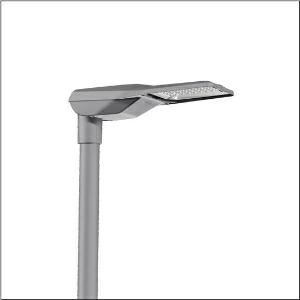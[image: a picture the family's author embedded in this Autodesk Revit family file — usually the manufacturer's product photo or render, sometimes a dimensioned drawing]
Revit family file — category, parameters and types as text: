
# Revit family: streetlight_sl_21_iq_mini___st0_5a_5xe2b31g08gb_b1a9
name_source: partatom
category: Lighting Fixtures
units: mm (PartAtom-declared; Revit-internal decimal feet)

## family parameters
Cut with Voids When Loaded = No
Host = Face
Light Source = No
Part Type = Normal
Room Calculation Point = No
Round Connector Dimension = Use Diameter
Shared = No

## types (1)
- --- (1 x LED, 5680 lm, 37.1 W, 3000K)
    Apparent Load = 37 VA
    CIE Flux Codes = 41 75 97 100 100
    Color Rendering = 70
    Color Temperature = 3000K
    Default Elevation = 1800 mm
    Description = Streetlight SL 21 iQ mini, mast luminaire, primary light control with lens, of PMMA, primary optical cover: cover, of toughened safety glass, transparent, light distribution: ST0.5a, light emission: direct distribution, primary light characteristic: asymmetric, installation type: post-top, side-entry, LED, High Power LED, rated luminous flux: 5.680lm, luminous efficacy: 153lm/W, light colour: 730, colour temperature: 3000K, control: Street-Remote, Auto-Match, Temp-Guard, Lumen-Switch, Night-Set, Smart-Wire, Light-Fading, Desk-Remote (wireless, voltage-free reading and setting of iQ features in the workshop via application-optimized NFC function/RFID function), optimised constant luminous flux control (CLO 2.0), presetting dimming linear, mains connection: 220..240V, AC, 50/60Hz, start of lifetime: 37W, end of service life: 39W, reduction: 18W, luminaire housing, of diecast aluminium, powder-coated, Siteco® metallic grey (DB 702S), corrosivity category C5 mid according to DIN EN ISO 12944, please order mast flange separately, inclination adjustable: 0°, 5°, 10°, 15°, sealing non-destructively replaceable, multi-level sealing system, length: 628mm, width: 235mm, height: 110mm, mast flange for spigot size: 42mm (side-entry): 5XC10008XM4, 60/48mm (side-entry/post-top): 5XC10108XM2, 76/60mm (side-entry/post-top): 5XC10108XM1, protection rating (complete): IP66, insulation class (complete): insulation class II (safety insulation), certification: CE, ENEC, ENEC+, VDE, impact resistance: IK09, permissible operating ambient temperature for outdoor applications: -40..+50°C, standard-compliant lighting for roads and squares, packaging unit: 1 piece

Light Distribution: ST0.5a
    Height = 110 mm
    Lamp = 1 x LED
    Lamp Light Flux = 5680 lm
    Lamp Power = 37.1 W
    Lamp count = 1
    Length = 625 mm
    Luminous efficacy = 153 lm/W
    Manufacturer = Siteco
    ModVariant = No
    Model = 5XE2B31G08GB
    Number of Poles = 1
    OnlyDefault = Yes
    Power Factor = 1
    Product Name = Streetlight SL 21 iQ mini | ST0.5a
    Product group = mast luminaire | pylon top
    ProductGroupID = 6100
    Protection Class = Protection class II
    Protection Degree = IP 66
    RLX_Detail_Level = 1
    RLX_Emergency_Light_Flux = 0 lm
    RLX_Emergency_Type = 0
    RLX_Emergency_Type_DB = No
    RlxData = <blob elided: 103193 chars, md5=bbedcacb>
    Socket = socket
    Standby Power = 0 W
    System Light Flux = 5680 lm
    System Power = 37 W
    Type Comments = factory setting: luminous flux: 100 % | dim-lin: 254 | 385 mA
    Type Image = l_1003519.jpg
    URL = http://relux.com
    VarID = @adj_143851
    Voltage = 0 V
    Weight = 0.00 kg
    Width = 234 mm

## geometry (parser evidence)
native form markers: Blend x4, Sweep x10
no freeform markers — native parametric forms only
